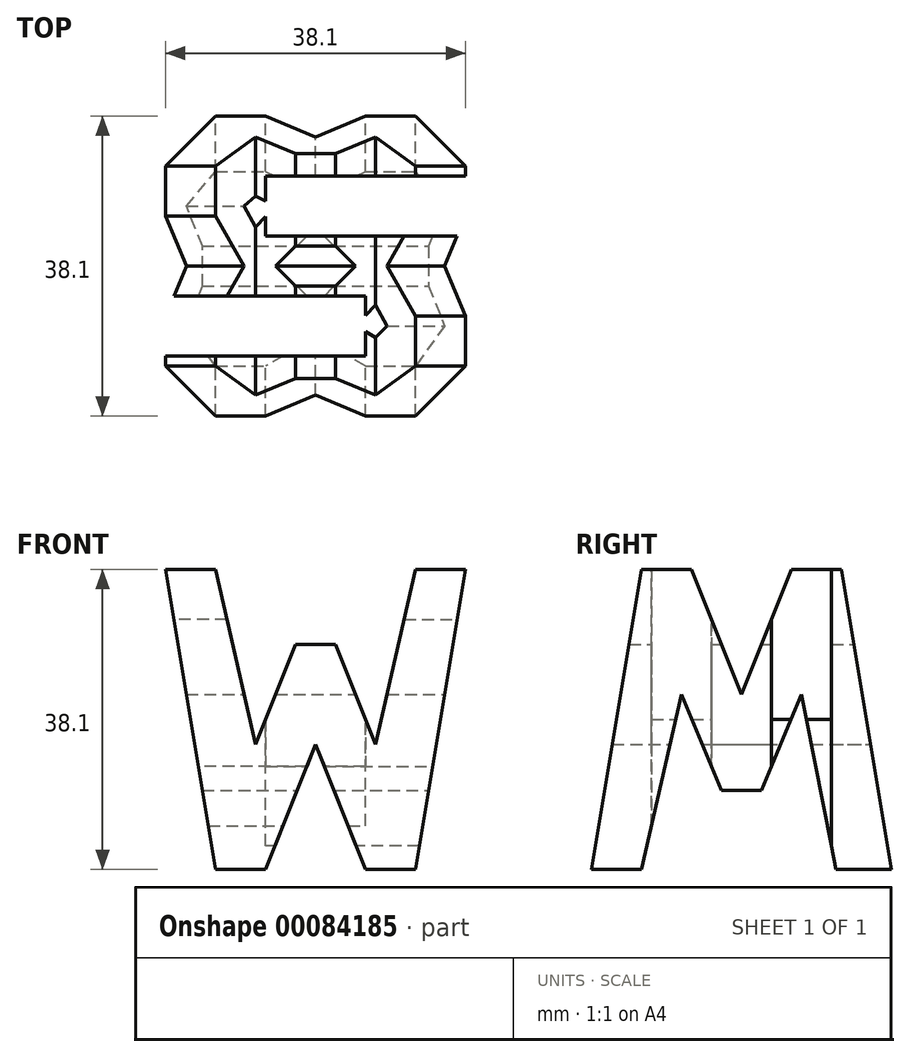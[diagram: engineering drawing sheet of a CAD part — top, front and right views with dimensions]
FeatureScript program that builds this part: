
annotation { "Feature Type Name" : "Feature", "Feature Type Description" : "" }
export const myFeature = defineFeature(function(context is Context, id is Id, definition is map)
    precondition{}
    {
        {
            var Q0;
            Q0=qCreatedBy(makeId("Front.planeOp"),FACE);
            var sketch = newSketch(context, id + "F0", { "sketchPlane" : qUnion([Q0])});
            skLineSegment(sketch, "E0", {"start": v(0, 0) * mm, "end": v(38.1, 0) * mm});
            skLineSegment(sketch, "E1", {"start": v(38.1, 0) * mm, "end": v(38.1, 38.1) * mm});
            skLineSegment(sketch, "E2", {"start": v(38.1, 38.1) * mm, "end": v(0, 38.1) * mm});
            skLineSegment(sketch, "E3", {"start": v(0, 38.1) * mm, "end": v(0, 0) * mm});
            skSolve(sketch);
        }
        {
            var Q0;
            Q0 = qSketchRegion(id + "F0", true);
            extrude(context, id + "F1", {"entities" : qUnion([Q0]), "depth" : 38.1 * mm});
        }
        {
            var Q0;
            Q0=qCreatedBy(makeId("Right.planeOp"),FACE);
            cPlane(context, id + "F2", {"entities" : qUnion([Q0]), "cplaneType" : CPlaneType.OFFSET, "offset" : 38.1 * mm, "width" : 152.4 * mm, "height" : 152.4 * mm});
        }
        {
            var Q0;
            Q0=qCreatedBy(makeId("Top.planeOp"),FACE);
            cPlane(context, id + "F3", {"entities" : qUnion([Q0]), "cplaneType" : CPlaneType.OFFSET, "offset" : 38.1 * mm, "width" : 152.4 * mm, "height" : 152.4 * mm});
        }
        {
            var Q0;
            Q0=qCreatedBy(makeId("Front.planeOp"),FACE);
            var sketch = newSketch(context, id + "F4", { "sketchPlane" : qUnion([Q0])});
            skLineSegment(sketch, "E4", {"start": v(0, 38.1) * mm, "end": v(6.35, 0) * mm});
            skLineSegment(sketch, "E5", {"start": v(6.35, 0) * mm, "end": v(12.7, 0) * mm});
            skLineSegment(sketch, "E6", {"start": v(12.7, 0) * mm, "end": v(19.05, 15.87) * mm});
            skLineSegment(sketch, "E7", {"start": v(19.05, 15.87) * mm, "end": v(25.4, 0) * mm});
            skLineSegment(sketch, "E8", {"start": v(25.4, 0) * mm, "end": v(31.75, 0) * mm});
            skLineSegment(sketch, "E9", {"start": v(31.75, 0) * mm, "end": v(38.1, 38.1) * mm});
            skLineSegment(sketch, "E10", {"start": v(38.1, 38.1) * mm, "end": v(31.75, 38.1) * mm});
            skLineSegment(sketch, "E11", {"start": v(31.75, 38.1) * mm, "end": v(26.67, 15.87) * mm});
            skLineSegment(sketch, "E12", {"start": v(26.67, 15.87) * mm, "end": v(21.6, 28.58) * mm});
            skLineSegment(sketch, "E13", {"start": v(21.6, 28.57) * mm, "end": v(16.51, 28.57) * mm});
            skLineSegment(sketch, "E14", {"start": v(16.51, 28.57) * mm, "end": v(11.43, 15.87) * mm});
            skLineSegment(sketch, "E15", {"start": v(11.43, 15.87) * mm, "end": v(6.35, 38.1) * mm});
            skLineSegment(sketch, "E16", {"start": v(6.35, 38.1) * mm, "end": v(0, 38.1) * mm});
            skLineSegment(sketch, "E17", {"start": v(0, 38.1) * mm, "end": v(0, 38.1) * mm});
            skLineSegment(sketch, "E18.bottom", {"start": v(0, 0) * mm, "end": v(38.1, 0) * mm});
            skLineSegment(sketch, "E18.top", {"start": v(0, 38.1) * mm, "end": v(38.1, 38.1) * mm});
            skLineSegment(sketch, "E18.left", {"start": v(0, 0) * mm, "end": v(0, 38.1) * mm});
            skLineSegment(sketch, "E18.right", {"start": v(38.1, 0) * mm, "end": v(38.1, 38.1) * mm});
            skSolve(sketch);
        }
        {
            var Q0;
            {var subQ0=sQuery(id+"F4.wireOp",EDGE,"E4");Q0=makeQuery(id+"F4.imprint","IMPRINT",FACE,{"disambiguationData":[TD([[makeQuery(id+"F4.imprint","IMPRINT",EDGE,{"derivedFrom":subQ0}),-1.0]])]});}
            var Q1;
            {var subQ1=sQuery(id+"F4.wireOp",EDGE,"E11");Q1=makeQuery(id+"F4.imprint","IMPRINT",FACE,{"disambiguationData":[TD([[makeQuery(id+"F4.imprint","IMPRINT",EDGE,{"derivedFrom":subQ1}),-1.0]])]});}
            var Q2;
            {var subQ0=sQuery(id+"F4.wireOp",EDGE,"E6");Q2=makeQuery(id+"F4.imprint","IMPRINT",FACE,{"disambiguationData":[TD([[makeQuery(id+"F4.imprint","IMPRINT",EDGE,{"derivedFrom":subQ0}),-1.0]])]});}
            var Q3;
            {var subQ0=sQuery(id+"F4.wireOp",EDGE,"E9");Q3=makeQuery(id+"F4.imprint","IMPRINT",FACE,{"disambiguationData":[TD([[makeQuery(id+"F4.imprint","IMPRINT",EDGE,{"derivedFrom":subQ0}),-1.0]])]});}
            extrude(context, id + "F5", {"entities" : qUnion([Q0, Q1, Q2, Q3]), "operationType" : NewBodyOperationType.REMOVE, "depth" : 38.1 * mm});
        }
        {
            var Q0;
            Q0=qCreatedBy(id+"F2.planeOp",FACE);
            var sketch = newSketch(context, id + "F6", { "sketchPlane" : qUnion([Q0])});
            skLineSegment(sketch, "E19", {"start": v(0, 0) * mm, "end": v(0, 38.1) * mm});
            skLineSegment(sketch, "E20", {"start": v(0, 38.1) * mm, "end": v(-38.1, 38.1) * mm});
            skLineSegment(sketch, "E21", {"start": v(-38.1, 38.1) * mm, "end": v(-38.1, 0) * mm});
            skLineSegment(sketch, "E22", {"start": v(-38.1, 0) * mm, "end": v(0, 0) * mm});
            skLineSegment(sketch, "E23", {"start": v(-38.1, 0) * mm, "end": v(-31.75, 38.1) * mm});
            skLineSegment(sketch, "E24", {"start": v(-31.75, 38.1) * mm, "end": v(-25.4, 38.1) * mm});
            skLineSegment(sketch, "E25", {"start": v(-25.4, 38.1) * mm, "end": v(-19.05, 22.23) * mm});
            skLineSegment(sketch, "E26", {"start": v(-19.05, 22.23) * mm, "end": v(-12.7, 38.1) * mm});
            skLineSegment(sketch, "E27", {"start": v(-12.7, 38.1) * mm, "end": v(-6.35, 38.1) * mm});
            skLineSegment(sketch, "E28", {"start": v(-6.35, 38.1) * mm, "end": v(0, 0) * mm});
            skLineSegment(sketch, "E29", {"start": v(-31.75, 0) * mm, "end": v(-26.67, 22.23) * mm});
            skLineSegment(sketch, "E30", {"start": v(-26.67, 22.23) * mm, "end": v(-21.59, 10.05) * mm});
            skLineSegment(sketch, "E31", {"start": v(-21.59, 10.05) * mm, "end": v(-16.5, 10.05) * mm});
            skLineSegment(sketch, "E32", {"start": v(-16.5, 10.05) * mm, "end": v(-11.43, 22.22) * mm});
            skLineSegment(sketch, "E33", {"start": v(-11.43, 22.22) * mm, "end": v(-7.03, 0) * mm});
            skSolve(sketch);
        }
        {
            var Q0;
            {var subQ0=sQuery(id+"F6.wireOp",EDGE,"E21");Q0=makeQuery(id+"F6.imprint","IMPRINT",FACE,{"disambiguationData":[TD([[makeQuery(id+"F6.imprint","IMPRINT",EDGE,{"derivedFrom":subQ0}),1.0]])]});}
            var Q1;
            {var subQ0=sQuery(id+"F6.wireOp",EDGE,"E25");Q1=makeQuery(id+"F6.imprint","IMPRINT",FACE,{"disambiguationData":[TD([[makeQuery(id+"F6.imprint","IMPRINT",EDGE,{"derivedFrom":subQ0}),1.0]])]});}
            var Q2;
            {var subQ0=sQuery(id+"F6.wireOp",EDGE,"E29");Q2=makeQuery(id+"F6.imprint","IMPRINT",FACE,{"disambiguationData":[TD([[makeQuery(id+"F6.imprint","IMPRINT",EDGE,{"derivedFrom":subQ0}),-1.0]])]});}
            var Q3;
            {var subQ0=sQuery(id+"F6.wireOp",EDGE,"E19");Q3=makeQuery(id+"F6.imprint","IMPRINT",FACE,{"disambiguationData":[TD([[makeQuery(id+"F6.imprint","IMPRINT",EDGE,{"derivedFrom":subQ0}),1.0]])]});}
            extrude(context, id + "F7", {"entities" : qUnion([Q0, Q1, Q2, Q3]), "operationType" : NewBodyOperationType.REMOVE, "oppositeDirection" : true, "depth" : 38.1 * mm});
        }
        {
            var Q0;
            Q0=qCreatedBy(id+"F3.planeOp",FACE);
            var sketch = newSketch(context, id + "F8", { "sketchPlane" : qUnion([Q0])});
            skLineSegment(sketch, "E34", {"start": v(0, 0) * mm, "end": v(0, -38.1) * mm});
            skLineSegment(sketch, "E35", {"start": v(0, -38.1) * mm, "end": v(38.1, -38.1) * mm});
            skLineSegment(sketch, "E36", {"start": v(38.1, -38.1) * mm, "end": v(38.1, 0) * mm});
            skLineSegment(sketch, "E37", {"start": v(38.1, 0) * mm, "end": v(0, 0) * mm});
            skLineSegment(sketch, "E38", {"start": v(38.1, -15.24) * mm, "end": v(12.7, -15.24) * mm});
            skLineSegment(sketch, "E39", {"start": v(12.7, -15.24) * mm, "end": v(12.7, -7.62) * mm});
            skLineSegment(sketch, "E40", {"start": v(12.7, -7.62) * mm, "end": v(38.1, -7.62) * mm});
            skLineSegment(sketch, "E41", {"start": v(0, -22.86) * mm, "end": v(25.4, -22.86) * mm});
            skLineSegment(sketch, "E42", {"start": v(25.4, -22.86) * mm, "end": v(25.4, -30.48) * mm});
            skLineSegment(sketch, "E43", {"start": v(25.4, -30.48) * mm, "end": v(0, -30.48) * mm});
            skSolve(sketch);
        }
        {
            var Q0;
            {var subQ0=sQuery(id+"F8.wireOp",EDGE,"E41");Q0=makeQuery(id+"F8.imprint","IMPRINT",FACE,{"disambiguationData":[TD([[makeQuery(id+"F8.imprint","IMPRINT",EDGE,{"derivedFrom":subQ0}),-1.0]])]});}
            var Q1;
            {var subQ0=sQuery(id+"F8.wireOp",EDGE,"E38");Q1=makeQuery(id+"F8.imprint","IMPRINT",FACE,{"disambiguationData":[TD([[makeQuery(id+"F8.imprint","IMPRINT",EDGE,{"derivedFrom":subQ0}),-1.0]])]});}
            extrude(context, id + "F9", {"entities" : qUnion([Q0, Q1]), "operationType" : NewBodyOperationType.REMOVE, "oppositeDirection" : true, "depth" : 38.1 * mm});
        }
    });
